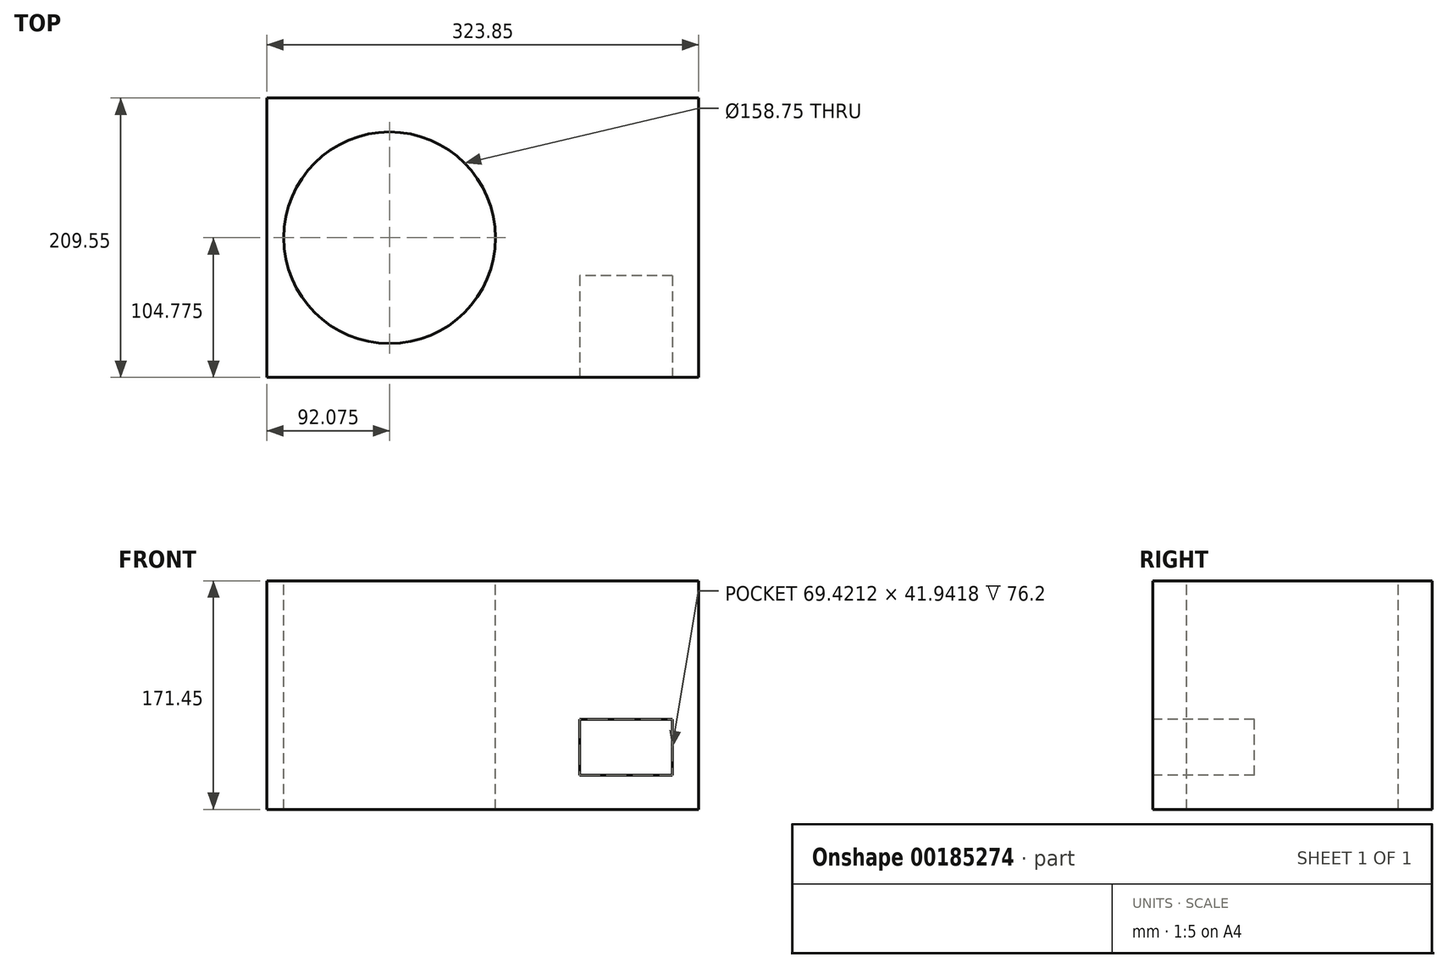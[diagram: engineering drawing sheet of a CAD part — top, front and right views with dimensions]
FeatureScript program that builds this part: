
annotation { "Feature Type Name" : "Feature", "Feature Type Description" : "" }
export const myFeature = defineFeature(function(context is Context, id is Id, definition is map)
    precondition{}
    {
        {
            var Q0;
            Q0=qCreatedBy(makeId("Top.planeOp"),FACE);
            var sketch = newSketch(context, id + "F0", { "sketchPlane" : qUnion([Q0])});
            skLineSegment(sketch, "E0.bottom", {"start": v(0, 0) * mm, "end": v(323.85, 0) * mm});
            skLineSegment(sketch, "E0.top", {"start": v(0, 209.55) * mm, "end": v(323.85, 209.55) * mm});
            skLineSegment(sketch, "E0.left", {"start": v(0, 0) * mm, "end": v(0, 209.55) * mm});
            skLineSegment(sketch, "E0.right", {"start": v(323.85, 0) * mm, "end": v(323.85, 209.55) * mm});
            skSolve(sketch);
        }
        {
            var Q0;
            Q0 = qSketchRegion(id + "F0", true);
            extrude(context, id + "F1", {"entities" : qUnion([Q0]), "depth" : 171.45 * mm});
        }
        {
            var Q0;
            Q0=makeQuery(id+"F1.opExtrude","CAP_FACE",FACE,{"disambiguationData":[OSD([sQuery(id+"F0.wireOp",EDGE,"E0.bottom"),sQuery(id+"F0.wireOp",EDGE,"E0.top"),sQuery(id+"F0.wireOp",EDGE,"E0.left"),sQuery(id+"F0.wireOp",EDGE,"E0.right")])],"isStart":false});
            var sketch = newSketch(context, id + "F2", { "sketchPlane" : qUnion([Q0])});
            skCircle(sketch, "E1", {"center": v(92.08, 104.78) * mm, "radius": 79.38 * mm});
            skSolve(sketch);
        }
        {
            var Q0;
            Q0 = qSketchRegion(id + "F2", true);
            extrude(context, id + "F3", {"entities" : qUnion([Q0]), "operationType" : NewBodyOperationType.REMOVE, "endBound" : BoundingType.THROUGH_ALL, "oppositeDirection" : true, "depth" : 25.4 * mm});
        }
        {
            var Q0;
            Q0=makeQuery(id+"F1.opExtrude","SWEPT_FACE",FACE,{"disambiguationData":[OSD([sQuery(id+"F0.wireOp",EDGE,"E0.bottom")])]});
            var sketch = newSketch(context, id + "F4", { "sketchPlane" : qUnion([Q0])});
            skLineSegment(sketch, "E2.bottom", {"start": v(304.18, 25.51) * mm, "end": v(234.76, 25.51) * mm});
            skLineSegment(sketch, "E2.top", {"start": v(304.18, 67.46) * mm, "end": v(234.76, 67.46) * mm});
            skLineSegment(sketch, "E2.left", {"start": v(304.18, 25.51) * mm, "end": v(304.18, 67.46) * mm});
            skLineSegment(sketch, "E2.right", {"start": v(234.76, 25.51) * mm, "end": v(234.76, 67.46) * mm});
            skSolve(sketch);
        }
        {
            var Q0;
            Q0 = qSketchRegion(id + "F4", true);
            extrude(context, id + "F5", {"entities" : qUnion([Q0]), "operationType" : NewBodyOperationType.REMOVE, "oppositeDirection" : true, "depth" : 76.2 * mm});
        }
    });
